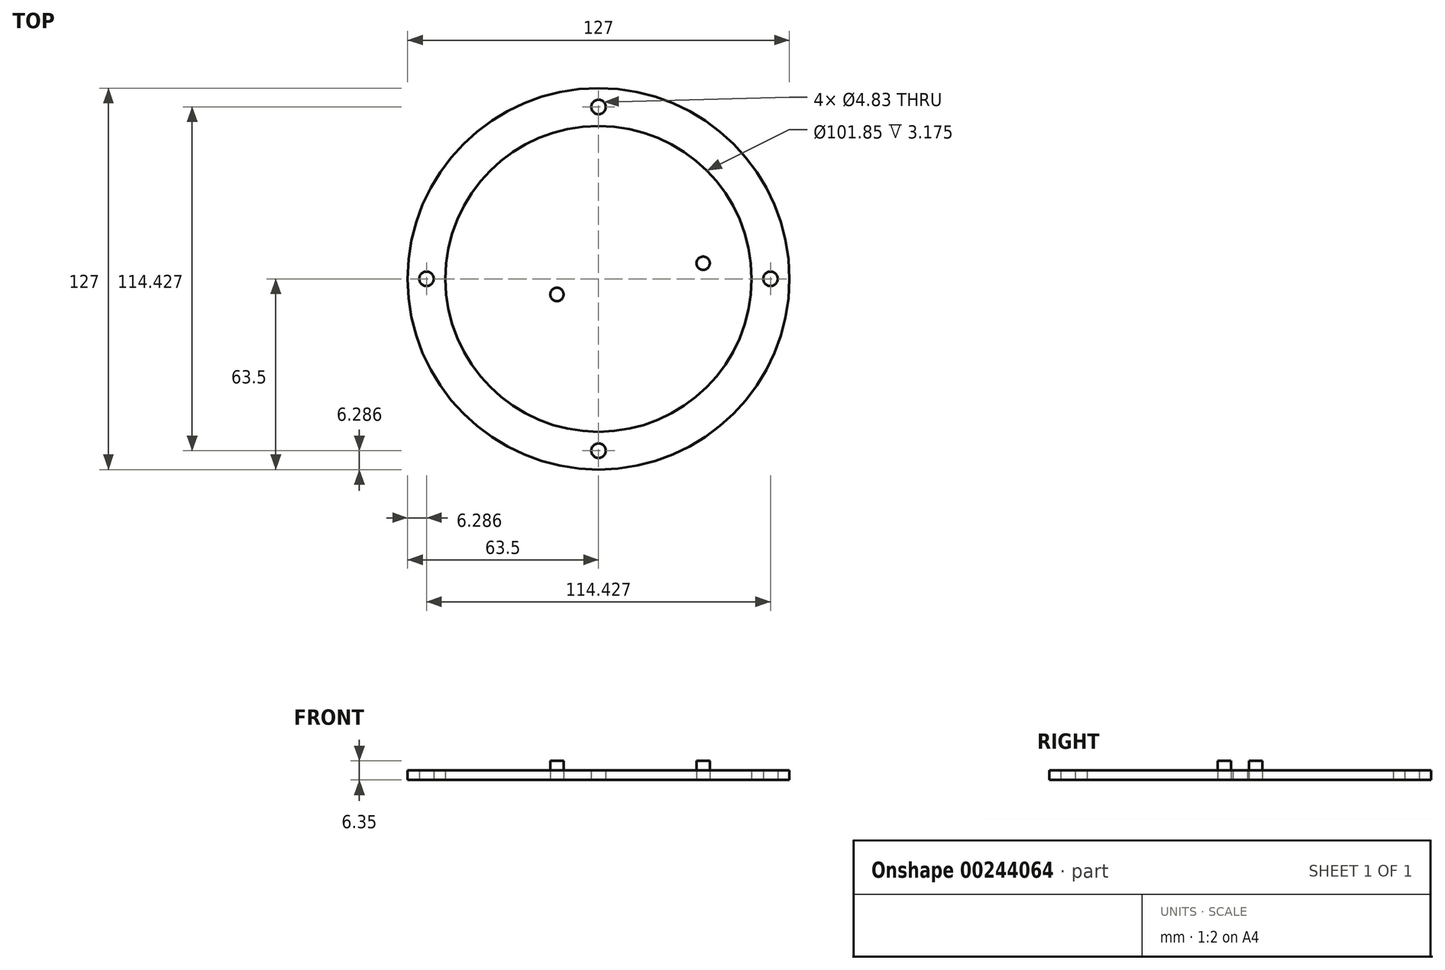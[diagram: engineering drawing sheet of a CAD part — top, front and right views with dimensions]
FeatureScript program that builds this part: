
annotation { "Feature Type Name" : "Feature", "Feature Type Description" : "" }
export const myFeature = defineFeature(function(context is Context, id is Id, definition is map)
    precondition{}
    {
        {
            var Q0;
            Q0=qCreatedBy(makeId("Top.planeOp"),FACE);
            var sketch = newSketch(context, id + "F0", { "sketchPlane" : qUnion([Q0])});
            skCircle(sketch, "E0", {"center": v(0, 0) * mm, "radius": 63.5 * mm});
            skCircle(sketch, "E1", {"center": v(0, 0) * mm, "radius": 50.8 * mm, "construction": true});
            skCircle(sketch, "E2.0", {"center": v(0, 0) * mm, "radius": 44.45 * mm, "construction": true});
            skSolve(sketch);
        }
        {
            var Q0;
            Q0 = qSketchRegion(id + "F0", true);
            extrude(context, id + "F1", {"entities" : qUnion([Q0]), "depth" : 3.17 * mm});
        }
        {
            var Q0;
            Q0=makeQuery(id+"F1.opExtrude","CAP_FACE",FACE,{"disambiguationData":[OSD([sQuery(id+"F0.wireOp",EDGE,"E0")])],"isStart":false});
            var sketch = newSketch(context, id + "F2", { "sketchPlane" : qUnion([Q0])});
            skCircle(sketch, "E3.0", {"center": v(0, 0) * mm, "radius": 50.8 * mm, "construction": true});
            skCircle(sketch, "E4.0", {"center": v(0, 0) * mm, "radius": 44.45 * mm, "construction": true});
            skCircle(sketch, "E5.0.0", {"center": v(0, 0) * mm, "radius": 63.5 * mm});
            skCircle(sketch, "E6.0", {"center": v(0, 0) * mm, "radius": 50.93 * mm});
            skCircle(sketch, "E7.0", {"center": v(0, 0) * mm, "radius": 44.32 * mm});
            skSolve(sketch);
        }
        {
            var Q0;
            Q0=makeQuery(id+"F2.imprint","IMPRINT",FACE,{"disambiguationData":[TD([[makeQuery(id+"F2.imprint","IMPRINT",EDGE,{"derivedFrom":sQuery(id+"F2.wireOp",EDGE,"E5.0.0")}),1.0]])]});
            var Q1;
            Q1=makeQuery(id+"F2.imprint","IMPRINT",FACE,{"disambiguationData":[TD([[makeQuery(id+"F2.imprint","IMPRINT",EDGE,{"derivedFrom":sQuery(id+"F2.wireOp",EDGE,"E7.0")}),1.0]])]});
            extrude(context, id + "F3", {"entities" : qUnion([Q0, Q1]), "depth" : 3.17 * mm});
        }
        {
            var Q0;
            Q0=makeQuery(id+"F1.opExtrude","CAP_FACE",FACE,{"disambiguationData":[OSD([sQuery(id+"F0.wireOp",EDGE,"E0")])],"isStart":true});
            var sketch = newSketch(context, id + "F4", { "sketchPlane" : qUnion([Q0])});
            skLineSegment(sketch, "E8.bottom", {"start": v(30.82, 10.16) * mm, "end": v(-9.82, 10.16) * mm, "construction": true});
            skLineSegment(sketch, "E8.top", {"start": v(30.82, -10.16) * mm, "end": v(-9.82, -10.16) * mm, "construction": true});
            skLineSegment(sketch, "E8.left", {"start": v(30.82, 10.16) * mm, "end": v(30.82, -10.16) * mm, "construction": true});
            skLineSegment(sketch, "E8.right", {"start": v(-9.82, 10.16) * mm, "end": v(-9.82, -10.16) * mm, "construction": true});
            skPoint(sketch, "E8.middle", {"position": v(10.5, 0) * mm});
            skLineSegment(sketch, "E9", {"start": v(30.82, 10.16) * mm, "end": v(62.68, 10.16) * mm, "construction": true});
            skLineSegment(sketch, "E10.0", {"start": v(31.33, 10.67) * mm, "end": v(-10.33, 10.67) * mm});
            skLineSegment(sketch, "E10.1", {"start": v(31.33, 10.67) * mm, "end": v(31.33, -10.67) * mm});
            skLineSegment(sketch, "E10.2", {"start": v(31.33, -10.67) * mm, "end": v(-10.33, -10.67) * mm});
            skLineSegment(sketch, "E10.3", {"start": v(-10.33, 10.67) * mm, "end": v(-10.33, -10.67) * mm});
            skCircle(sketch, "E11", {"center": v(34.82, 5.2) * mm, "radius": 2.22 * mm});
            skCircle(sketch, "E12.MirrorC", {"center": v(34.82, -5.2) * mm, "radius": 2.22 * mm});
            skLineSegment(sketch, "E13", {"start": v(10.5, 0) * mm, "end": v(10.5, 17.86) * mm, "construction": true});
            skCircle(sketch, "E14.MirrorC", {"center": v(-13.82, 5.2) * mm, "radius": 2.22 * mm});
            skCircle(sketch, "E15.MirrorC", {"center": v(-13.82, -5.2) * mm, "radius": 2.22 * mm});
            skCircle(sketch, "E16", {"center": v(-57.21, 0) * mm, "radius": 2.41 * mm});
            skCircle(sketch, "E17.0", {"center": v(0, 0) * mm, "radius": 50.93 * mm});
            skLineSegment(sketch, "E18", {"start": v(-57.21, 0) * mm, "end": v(-50.93, 0) * mm, "construction": true});
            skLineSegment(sketch, "E19", {"start": v(-57.21, 0) * mm, "end": v(-63.5, 0) * mm, "construction": true});
            skCircle(sketch, "E20.1.0", {"center": v(0, -57.21) * mm, "radius": 2.41 * mm});
            skCircle(sketch, "E20.2.0", {"center": v(57.21, 0) * mm, "radius": 2.41 * mm});
            skCircle(sketch, "E20.3.0", {"center": v(0, 57.21) * mm, "radius": 2.41 * mm});
            skSolve(sketch);
        }
        {
            var Q0;
            Q0=makeQuery(id+"F4.imprint","IMPRINT",FACE,{"disambiguationData":[TD([[makeQuery(id+"F4.imprint","IMPRINT",EDGE,{"derivedFrom":sQuery(id+"F4.wireOp",EDGE,"E10.0")}),1.0]])]});
            var Q1;
            Q1=makeQuery(id+"F4.imprint","IMPRINT",FACE,{"disambiguationData":[TD([[makeQuery(id+"F4.imprint","IMPRINT",EDGE,{"derivedFrom":sQuery(id+"F4.wireOp",EDGE,"E12.MirrorC")}),-1.0]])]});
            var Q2;
            Q2=makeQuery(id+"F4.imprint","IMPRINT",FACE,{"disambiguationData":[TD([[makeQuery(id+"F4.imprint","IMPRINT",EDGE,{"derivedFrom":sQuery(id+"F4.wireOp",EDGE,"E11")}),1.0]])]});
            var Q3;
            Q3=makeQuery(id+"F4.imprint","IMPRINT",FACE,{"disambiguationData":[TD([[makeQuery(id+"F4.imprint","IMPRINT",EDGE,{"derivedFrom":sQuery(id+"F4.wireOp",EDGE,"E14.MirrorC")}),-1.0]])]});
            var Q4;
            Q4=makeQuery(id+"F4.imprint","IMPRINT",FACE,{"disambiguationData":[TD([[makeQuery(id+"F4.imprint","IMPRINT",EDGE,{"derivedFrom":sQuery(id+"F4.wireOp",EDGE,"E15.MirrorC")}),1.0]])]});
            var Q5;
            Q5=makeQuery(id+"F4.imprint","IMPRINT",FACE,{"disambiguationData":[TD([[makeQuery(id+"F4.imprint","IMPRINT",EDGE,{"derivedFrom":sQuery(id+"F4.wireOp",EDGE,"E16")}),1.0]])]});
            var Q6;
            Q6=makeQuery(id+"F4.imprint","IMPRINT",FACE,{"disambiguationData":[TD([[makeQuery(id+"F4.imprint","IMPRINT",EDGE,{"derivedFrom":sQuery(id+"F4.wireOp",EDGE,"E20.1.0")}),1.0]])]});
            var Q7;
            Q7=makeQuery(id+"F4.imprint","IMPRINT",FACE,{"disambiguationData":[TD([[makeQuery(id+"F4.imprint","IMPRINT",EDGE,{"derivedFrom":sQuery(id+"F4.wireOp",EDGE,"E20.2.0")}),1.0]])]});
            var Q8;
            Q8=makeQuery(id+"F4.imprint","IMPRINT",FACE,{"disambiguationData":[TD([[makeQuery(id+"F4.imprint","IMPRINT",EDGE,{"derivedFrom":sQuery(id+"F4.wireOp",EDGE,"E20.3.0")}),1.0]])]});
            extrude(context, id + "F5", {"entities" : qUnion([Q0, Q1, Q2, Q3, Q4, Q5, Q6, Q7, Q8]), "operationType" : NewBodyOperationType.REMOVE, "endBound" : BoundingType.THROUGH_ALL, "oppositeDirection" : true, "depth" : 25.4 * mm});
        }
        {
            var Q0;
            Q0=makeQuery(id+"F4.imprint","IMPRINT",FACE,{"disambiguationData":[TD([[makeQuery(id+"F4.imprint","IMPRINT",EDGE,{"derivedFrom":sQuery(id+"F4.wireOp",EDGE,"E16")}),1.0]])]});
            var Q1;
            Q1=makeQuery(id+"F4.imprint","IMPRINT",FACE,{"disambiguationData":[TD([[makeQuery(id+"F4.imprint","IMPRINT",EDGE,{"derivedFrom":sQuery(id+"F4.wireOp",EDGE,"E20.3.0")}),1.0]])]});
            var Q2;
            Q2=makeQuery(id+"F4.imprint","IMPRINT",FACE,{"disambiguationData":[TD([[makeQuery(id+"F4.imprint","IMPRINT",EDGE,{"derivedFrom":sQuery(id+"F4.wireOp",EDGE,"E20.2.0")}),1.0]])]});
            var Q3;
            Q3=makeQuery(id+"F4.imprint","IMPRINT",FACE,{"disambiguationData":[TD([[makeQuery(id+"F4.imprint","IMPRINT",EDGE,{"derivedFrom":sQuery(id+"F4.wireOp",EDGE,"E20.1.0")}),1.0]])]});
            extrude(context, id + "F6", {"entities" : qUnion([Q0, Q1, Q2, Q3]), "operationType" : NewBodyOperationType.REMOVE, "oppositeDirection" : true, "depth" : 25.4 * mm});
        }
        {
            var Q0;
            Q0=makeQuery(id+"F3.opExtrude","CAP_FACE",FACE,{"disambiguationData":[OSD([sQuery(id+"F2.wireOp",EDGE,"E7.0")])],"isStart":false});
            var sketch = newSketch(context, id + "F7", { "sketchPlane" : qUnion([Q0])});
            skCircle(sketch, "E21", {"center": v(0, 0) * mm, "radius": 12.25 * mm});
            skSolve(sketch);
        }
        {
            var Q0;
            Q0 = qSketchRegion(id + "F7", true);
            extrude(context, id + "F8", {"entities" : qUnion([Q0]), "operationType" : NewBodyOperationType.REMOVE, "endBound" : BoundingType.THROUGH_ALL, "oppositeDirection" : true, "depth" : 25.4 * mm});
        }
        {
            var Q0;
            Q0=makeQuery(id+"F3.opExtrude","SWEPT_BODY",BODY,{"disambiguationData":[OSD([sQuery(id+"F2.wireOp",EDGE,"E5.0.0"),sQuery(id+"F2.wireOp",EDGE,"E6.0")])]});
            deleteBodies(context, id + "F9", {"entities" : qUnion([Q0])});
        }
    });
